# Revit family: Key Switch_Surface
name_source: partatom
category: Generic Models
revit_build: Autodesk Revit 2017 (Build: 20190508_0315(x64)
units: mm (PartAtom-declared; Revit-internal decimal feet)

## family parameters
Can host rebar = No
Cut with Voids When Loaded = No
Host = Face
Part Type = Normal
Room Calculation Point = No
Round Connector Dimension = Use Diameter
Shared = No

## types (1)
- Key Switch_Surface
    Alto = 100 mm  [stored 0.328084 ft]
    Ancho = 100 mm  [stored 0.328084 ft]
    Cerradura = Plastic, Opaque Grey
    Cuerpo = Plastic, Opaque White
    Default Elevation = 1219 mm
    Description = Switch con llave de superficie
    Fondo = 71 mm  [stored 0.23294 ft]
    Manufacturer = G-U
    Marco = Plastic, Opaque Grey
    Model = Spring-operated Key Switch
    Tipo = Switch con llave
    Type Comments = Switch con llave de superficie
    URL = http://www.automatics.cl

note: [stored X ft] marks values corroborated as IEEE doubles in the binary element streams (Revit-internal decimal feet)

## geometry (parser evidence)
native form markers: Sweep x2
no freeform markers — native parametric forms only
